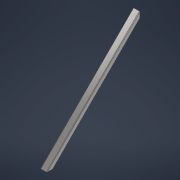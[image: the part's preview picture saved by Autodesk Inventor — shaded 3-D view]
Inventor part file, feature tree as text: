
AUTODESK INVENTOR PART (.ipt)
format: ipt  version: 2021 (Build 250183000, 183)  size: 120,832 bytes
history: native  units: mm
features: sweep x1, fillet x1, mirror x1, split x1, other x1, sketch x1
ambient origin geometry x8: Origin, YZ Plane, XZ Plane, XY Plane, X Axis, Y Axis, Z Axis, Center Point
bodies: Solid1 (feature_tree)
feature tree (6):
  sweep  "Sweep1"
  fillet  "Fillet1"  Radius=25.0mm
  mirror  "mirrored45"
  split  "Split1"
  other  "profile"
  sketch  "3D Sketch1"
